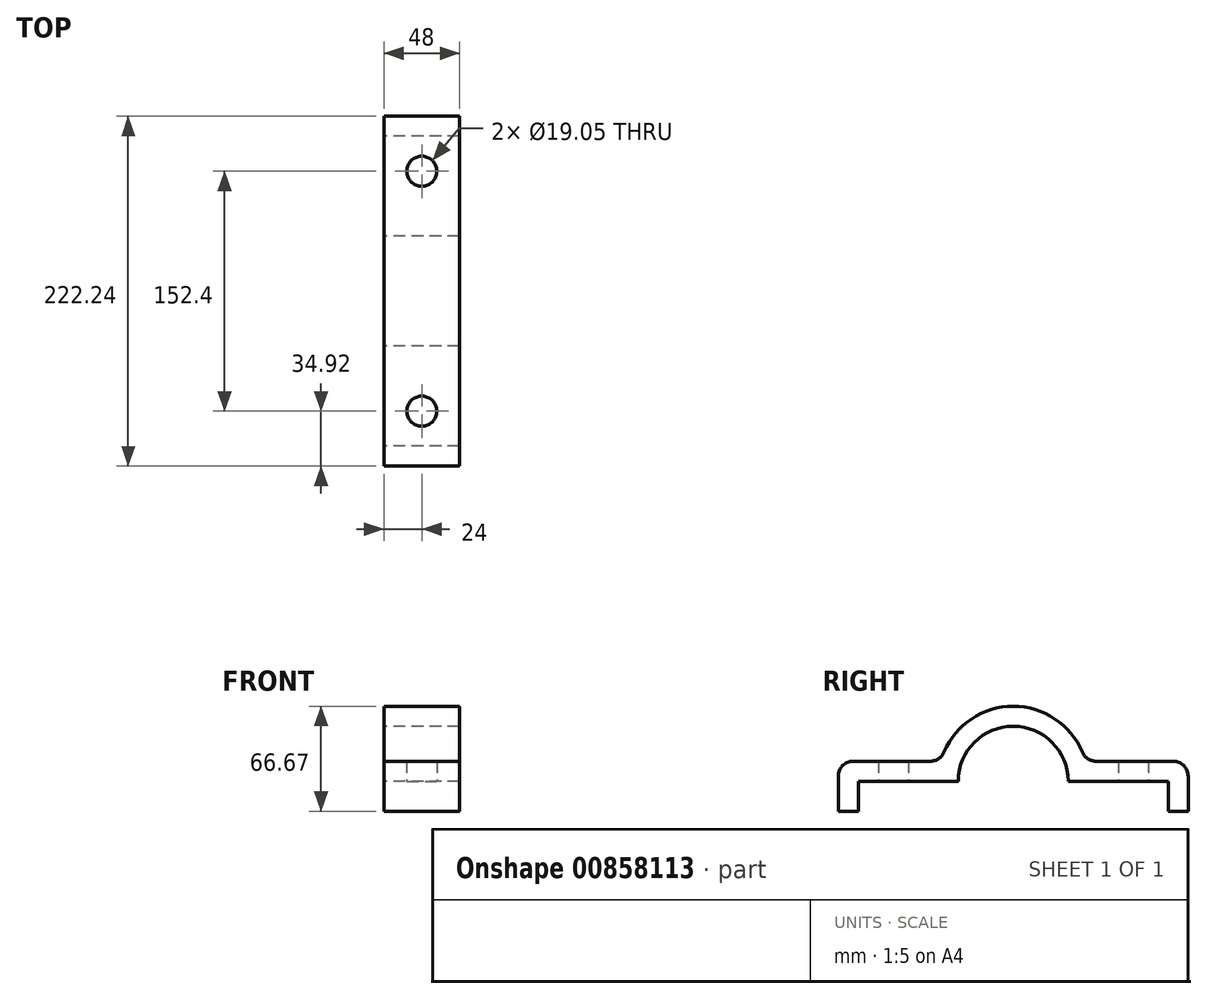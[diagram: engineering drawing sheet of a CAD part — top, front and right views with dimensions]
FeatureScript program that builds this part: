
annotation { "Feature Type Name" : "Feature", "Feature Type Description" : "" }
export const myFeature = defineFeature(function(context is Context, id is Id, definition is map)
    precondition{}
    {
        {
            var Q0;
            Q0=qCreatedBy(makeId("Right.planeOp"),FACE);
            var sketch = newSketch(context, id + "F0", { "sketchPlane" : qUnion([Q0])});
            skArc(sketch, "E0", {"start": v(34.93, 0) * mm, "mid": v(0, 34.93) * mm, "end": v(-34.93, 0) * mm});
            skLineSegment(sketch, "E1.bottom", {"start": v(-98.43, 0) * mm, "end": v(-34.93, 0) * mm});
            skLineSegment(sketch, "E1.top", {"start": v(-98.42, 12.7) * mm, "end": v(-45.9, 12.7) * mm});
            skLineSegment(sketch, "E1.left", {"start": v(-98.43, 0) * mm, "end": v(-98.43, 12.7) * mm});
            skLineSegment(sketch, "E1.right", {"start": v(98.43, 0) * mm, "end": v(98.43, 12.7) * mm});
            skLineSegment(sketch, "E2.bottom", {"start": v(98.43, 12.7) * mm, "end": v(87.43, 12.7) * mm});
            skArc(sketch, "E3.0", {"start": v(45.9, 12.7) * mm, "mid": v(0, 47.63) * mm, "end": v(-45.9, 12.7) * mm});
            skLineSegment(sketch, "E4.trimOffspring", {"start": v(34.93, 0) * mm, "end": v(98.43, 0) * mm});
            skLineSegment(sketch, "E5.trimOffspring", {"start": v(45.9, 12.7) * mm, "end": v(98.43, 12.7) * mm});
            skSolve(sketch);
        }
        {
            var Q0;
            {var subQ0=sQuery(id+"F0.wireOp",EDGE,"E1.left");Q0=makeQuery(id+"F0.imprint","IMPRINT",FACE,{"disambiguationData":[TD([[makeQuery(id+"F0.imprint","IMPRINT",EDGE,{"derivedFrom":subQ0}),-1.0]])]});}
            var Q1;
            {var subQ0=sQuery(id+"F0.wireOp",EDGE,"E1.top");var subQ1=sQuery(id+"F0.wireOp",EDGE,"E0");var subQ2=makeQuery(id+"F0.imprint","INTERSECT",VERTEX,{"disambiguationData":[OD(1.0)],"derivedFrom":[subQ1,subQ0]});Q1=makeQuery(id+"F0.imprint","IMPRINT",FACE,{"disambiguationData":[TD([[makeQuery(id+"F0.imprint","IMPRINT",EDGE,{"disambiguationData":[TD([[subQ2,-1.0]])],"derivedFrom":subQ1}),-1.0]])]});}
            var Q2;
            {var subQ0=sQuery(id+"F0.wireOp",EDGE,"E1.top");var subQ1=sQuery(id+"F0.wireOp",EDGE,"E0");var subQ2=makeQuery(id+"F0.imprint","INTERSECT",VERTEX,{"disambiguationData":[OD(0.0)],"derivedFrom":[subQ1,subQ0]});Q2=makeQuery(id+"F0.imprint","IMPRINT",FACE,{"disambiguationData":[TD([[makeQuery(id+"F0.imprint","IMPRINT",EDGE,{"disambiguationData":[TD([[subQ2,-1.0]])],"derivedFrom":subQ1}),-1.0]])]});}
            var Q3;
            {var subQ0=sQuery(id+"F0.wireOp",EDGE,"E1.top");var subQ1=sQuery(id+"F0.wireOp",EDGE,"E0");var subQ2=makeQuery(id+"F0.imprint","INTERSECT",VERTEX,{"disambiguationData":[OD(0.0)],"derivedFrom":[subQ1,subQ0]});Q3=makeQuery(id+"F0.imprint","IMPRINT",FACE,{"disambiguationData":[TD([[makeQuery(id+"F0.imprint","IMPRINT",EDGE,{"disambiguationData":[TD([[subQ2,1.0]])],"derivedFrom":subQ1}),-1.0]])]});}
            var Q4;
            {var subQ4=sQuery(id+"F0.wireOp",EDGE,"E1.right");Q4=makeQuery(id+"F0.imprint","IMPRINT",FACE,{"disambiguationData":[TD([[makeQuery(id+"F0.imprint","IMPRINT",EDGE,{"derivedFrom":subQ4}),1.0]])]});}
            var Q5;
            Q5=makeQuery(id+"F0.imprint","IMPRINT",FACE,{"disambiguationData":[TD([[makeQuery(id+"F0.imprint","IMPRINT",EDGE,{"derivedFrom":sQuery(id+"F0.wireOp",EDGE,"E2.bottom")}),-1.0]])]});
            extrude(context, id + "F1", {"entities" : qUnion([Q0, Q1, Q2, Q3, Q4, Q5]), "endBound" : BoundingType.SYMMETRIC, "depth" : 48 * mm, "offsetDistance" : 25.4 * mm});
        }
        {
            var Q0;
            Q0=makeQuery(id+"F1.opExtrude","SWEPT_FACE",FACE,{"disambiguationData":[OSD([sQuery(id+"F0.wireOp",EDGE,"E1.left")])]});
            var sketch = newSketch(context, id + "F2", { "sketchPlane" : qUnion([Q0])});
            skLineSegment(sketch, "E6.bottom", {"start": v(-24, 12.7) * mm, "end": v(24, 12.7) * mm});
            skLineSegment(sketch, "E6.top", {"start": v(-24, -19.05) * mm, "end": v(24, -19.05) * mm});
            skLineSegment(sketch, "E6.left", {"start": v(-24, 12.7) * mm, "end": v(-24, -19.05) * mm});
            skLineSegment(sketch, "E6.right", {"start": v(24, 12.7) * mm, "end": v(24, -19.05) * mm});
            skSolve(sketch);
        }
        {
            var Q0;
            {var subQ0=sQuery(id+"F2.wireOp",EDGE,"E6.bottom");Q0=makeQuery(id+"F2.imprint","IMPRINT",FACE,{"disambiguationData":[TD([[makeQuery(id+"F2.imprint","IMPRINT",EDGE,{"derivedFrom":subQ0}),1.0]])]});}
            var Q1;
            {var subQ0=sQuery(id+"F2.wireOp",EDGE,"E6.top");Q1=makeQuery(id+"F2.imprint","IMPRINT",FACE,{"disambiguationData":[TD([[makeQuery(id+"F2.imprint","IMPRINT",EDGE,{"derivedFrom":subQ0}),1.0]])]});}
            extrude(context, id + "F3", {"entities" : qUnion([Q0, Q1]), "operationType" : NewBodyOperationType.ADD, "depth" : 12.7 * mm, "offsetDistance" : 25.4 * mm});
        }
        {
            var Q0;
            Q0=makeQuery(id+"F3.opExtrude","CAP_EDGE",EDGE,{"disambiguationData":[OSD([sQuery(id+"F2.wireOp",EDGE,"E6.bottom")])],"isStart":false});
            fillet(context, id + "F4", {"entities" : qUnion([Q0]), "radius" : 9.52 * mm, "tangentPropagation" : true, "allowEdgeOverflow" : false});
        }
        {
            var Q0;
            Q0=makeQuery(id+"F1.opExtrude","SWEPT_FACE",FACE,{"disambiguationData":[OSD([sQuery(id+"F0.wireOp",EDGE,"E1.right")])]});
            var sketch = newSketch(context, id + "F5", { "sketchPlane" : qUnion([Q0])});
            skLineSegment(sketch, "E7.bottom", {"start": v(-24, 12.7) * mm, "end": v(24, 12.7) * mm});
            skLineSegment(sketch, "E7.top", {"start": v(-24, 0) * mm, "end": v(24, 0) * mm});
            skLineSegment(sketch, "E7.left", {"start": v(-24, 12.7) * mm, "end": v(-24, 0) * mm});
            skLineSegment(sketch, "E7.right", {"start": v(24, 12.7) * mm, "end": v(24, 0) * mm});
            skLineSegment(sketch, "E8.top", {"start": v(-24, -19.05) * mm, "end": v(24, -19.05) * mm});
            skLineSegment(sketch, "E8.left", {"start": v(-24, 0) * mm, "end": v(-24, -19.05) * mm});
            skLineSegment(sketch, "E8.right", {"start": v(24, 0) * mm, "end": v(24, -19.05) * mm});
            skSolve(sketch);
        }
        {
            var Q0;
            {var subQ0=sQuery(id+"F0.wireOp",EDGE,"E1.top");var subQ1=sQuery(id+"F0.wireOp",EDGE,"719fa735-c335-499d-85ab-ea83bd742e73");Q0=makeQuery(id+"F1.opExtrude","SWEPT_EDGE",EDGE,{"disambiguationData":[OSD([subQ1,subQ0]),TDD([makeQuery(id+"F0.imprint","INTERSECT",VERTEX,{"disambiguationData":[OD(1.0)],"derivedFrom":[subQ1,subQ0]})])]});}
            fillet(context, id + "F6", {"entities" : qUnion([Q0]), "radius" : 9.52 * mm, "tangentPropagation" : true, "allowEdgeOverflow" : false});
        }
        {
            var Q0;
            {var subQ0=sQuery(id+"F0.wireOp",EDGE,"E1.bottom");var subQ1=makeQuery(id+"F0.imprint","INTERSECT",VERTEX,{"disambiguationData":[OD(1.0)],"derivedFrom":[sQuery(id+"F0.wireOp",EDGE,"719fa735-c335-499d-85ab-ea83bd742e73"),subQ0]});Q0=makeQuery(id+"F1.opExtrude","SWEPT_FACE",FACE,{"disambiguationData":[OSD([subQ0]),TDD([makeQuery(id+"F0.imprint","IMPRINT",EDGE,{"disambiguationData":[TD([[makeQuery(id+"F0.imprint","INTERSECT",VERTEX,{"derivedFrom":[subQ0,sQuery(id+"F0.wireOp",EDGE,"E1.left")]}),-1.0]])],"derivedFrom":subQ0}),makeQuery(id+"F0.imprint","IMPRINT",EDGE,{"disambiguationData":[TD([[subQ1,-1.0]])],"derivedFrom":subQ0})])]});}
            var sketch = newSketch(context, id + "F7", { "sketchPlane" : qUnion([Q0])});
            skLineSegment(sketch, "E9", {"start": v(0, 34.93) * mm, "end": v(0, 76.2) * mm});
            skCircle(sketch, "E10", {"center": v(0, 76.2) * mm, "radius": 9.53 * mm});
            skSolve(sketch);
        }
        {
            var Q0;
            Q0=makeQuery(id+"F7.imprint","IMPRINT",FACE,{"disambiguationData":[TD([[makeQuery(id+"F7.imprint","IMPRINT",EDGE,{"derivedFrom":sQuery(id+"F7.wireOp",EDGE,"E10")}),1.0]])]});
            extrude(context, id + "F8", {"entities" : qUnion([Q0]), "operationType" : NewBodyOperationType.REMOVE, "oppositeDirection" : true, "depth" : 47.5 * mm, "offsetDistance" : 25.4 * mm});
        }
        {
            var Q0;
            {var subQ0=sQuery(id+"F0.wireOp",EDGE,"E1.bottom");var subQ1=makeQuery(id+"F0.imprint","INTERSECT",VERTEX,{"disambiguationData":[OD(0.0)],"derivedFrom":[sQuery(id+"F0.wireOp",EDGE,"719fa735-c335-499d-85ab-ea83bd742e73"),subQ0]});Q0=makeQuery(id+"F1.opExtrude","SWEPT_FACE",FACE,{"disambiguationData":[OSD([subQ0]),TDD([makeQuery(id+"F0.imprint","IMPRINT",EDGE,{"disambiguationData":[TD([[subQ1,1.0]])],"derivedFrom":subQ0}),makeQuery(id+"F0.imprint","IMPRINT",EDGE,{"disambiguationData":[TD([[makeQuery(id+"F0.imprint","INTERSECT",VERTEX,{"derivedFrom":[subQ0,sQuery(id+"F0.wireOp",EDGE,"E1.right")]}),1.0]])],"derivedFrom":subQ0})])]});}
            var sketch = newSketch(context, id + "F9", { "sketchPlane" : qUnion([Q0])});
            skLineSegment(sketch, "E11", {"start": v(0, 34.92) * mm, "end": v(0, -6.35) * mm});
            skCircle(sketch, "E12", {"center": v(0, -6.35) * mm, "radius": 9.53 * mm});
            skSolve(sketch);
        }
        {
            var Q0;
            Q0=makeQuery(id+"F9.imprint","IMPRINT",FACE,{"disambiguationData":[TD([[makeQuery(id+"F9.imprint","IMPRINT",EDGE,{"derivedFrom":sQuery(id+"F9.wireOp",EDGE,"E12")}),1.0]])]});
            extrude(context, id + "F10", {"entities" : qUnion([Q0]), "operationType" : NewBodyOperationType.REMOVE, "oppositeDirection" : true, "depth" : 25.4 * mm, "offsetDistance" : 25.4 * mm});
        }
        {
            var Q0;
            Q0=makeQuery(id+"F5.imprint","IMPRINT",FACE,{"disambiguationData":[TD([[makeQuery(id+"F5.imprint","IMPRINT",EDGE,{"derivedFrom":sQuery(id+"F5.wireOp",EDGE,"E7.top")}),-1.0]])]});
            var Q1;
            Q1=makeQuery(id+"F5.imprint","IMPRINT",FACE,{"disambiguationData":[TD([[makeQuery(id+"F5.imprint","IMPRINT",EDGE,{"derivedFrom":sQuery(id+"F5.wireOp",EDGE,"E7.bottom")}),-1.0]])]});
            extrude(context, id + "F11", {"entities" : qUnion([Q0, Q1]), "operationType" : NewBodyOperationType.ADD, "depth" : 12.7 * mm, "offsetDistance" : 25.4 * mm});
        }
        {
            var Q0;
            Q0=makeQuery(id+"F11.opExtrude","CAP_EDGE",EDGE,{"disambiguationData":[OSD([sQuery(id+"F5.wireOp",EDGE,"E7.bottom")])],"isStart":false});
            fillet(context, id + "F12", {"entities" : qUnion([Q0]), "radius" : 9.52 * mm, "tangentPropagation" : true, "allowEdgeOverflow" : false});
        }
        {
            var Q0;
            Q0=makeQuery(id+"F1.opExtrude","SWEPT_EDGE",EDGE,{"disambiguationData":[OSD([sQuery(id+"F0.wireOp",EDGE,"E3.0"),sQuery(id+"F0.wireOp",EDGE,"E5.trimOffspring")])]});
            fillet(context, id + "F13", {"entities" : qUnion([Q0]), "radius" : 9.52 * mm, "tangentPropagation" : true, "allowEdgeOverflow" : false});
        }
        {
            var Q0;
            Q0=makeQuery(id+"F1.opExtrude","SWEPT_FACE",FACE,{"disambiguationData":[OSD([sQuery(id+"F0.wireOp",EDGE,"E4.trimOffspring")])]});
            var sketch = newSketch(context, id + "F14", { "sketchPlane" : qUnion([Q0])});
            skLineSegment(sketch, "E13", {"start": v(0, -34.93) * mm, "end": v(0, -76.2) * mm});
            skCircle(sketch, "E14", {"center": v(0, -76.2) * mm, "radius": 9.53 * mm});
            skSolve(sketch);
        }
        {
            var Q0;
            Q0=makeQuery(id+"F14.imprint","IMPRINT",FACE,{"disambiguationData":[TD([[makeQuery(id+"F14.imprint","IMPRINT",EDGE,{"derivedFrom":sQuery(id+"F14.wireOp",EDGE,"E14")}),1.0]])]});
            extrude(context, id + "F15", {"entities" : qUnion([Q0]), "operationType" : NewBodyOperationType.REMOVE, "oppositeDirection" : true, "depth" : 25.4 * mm, "offsetDistance" : 25.4 * mm});
        }
    });
